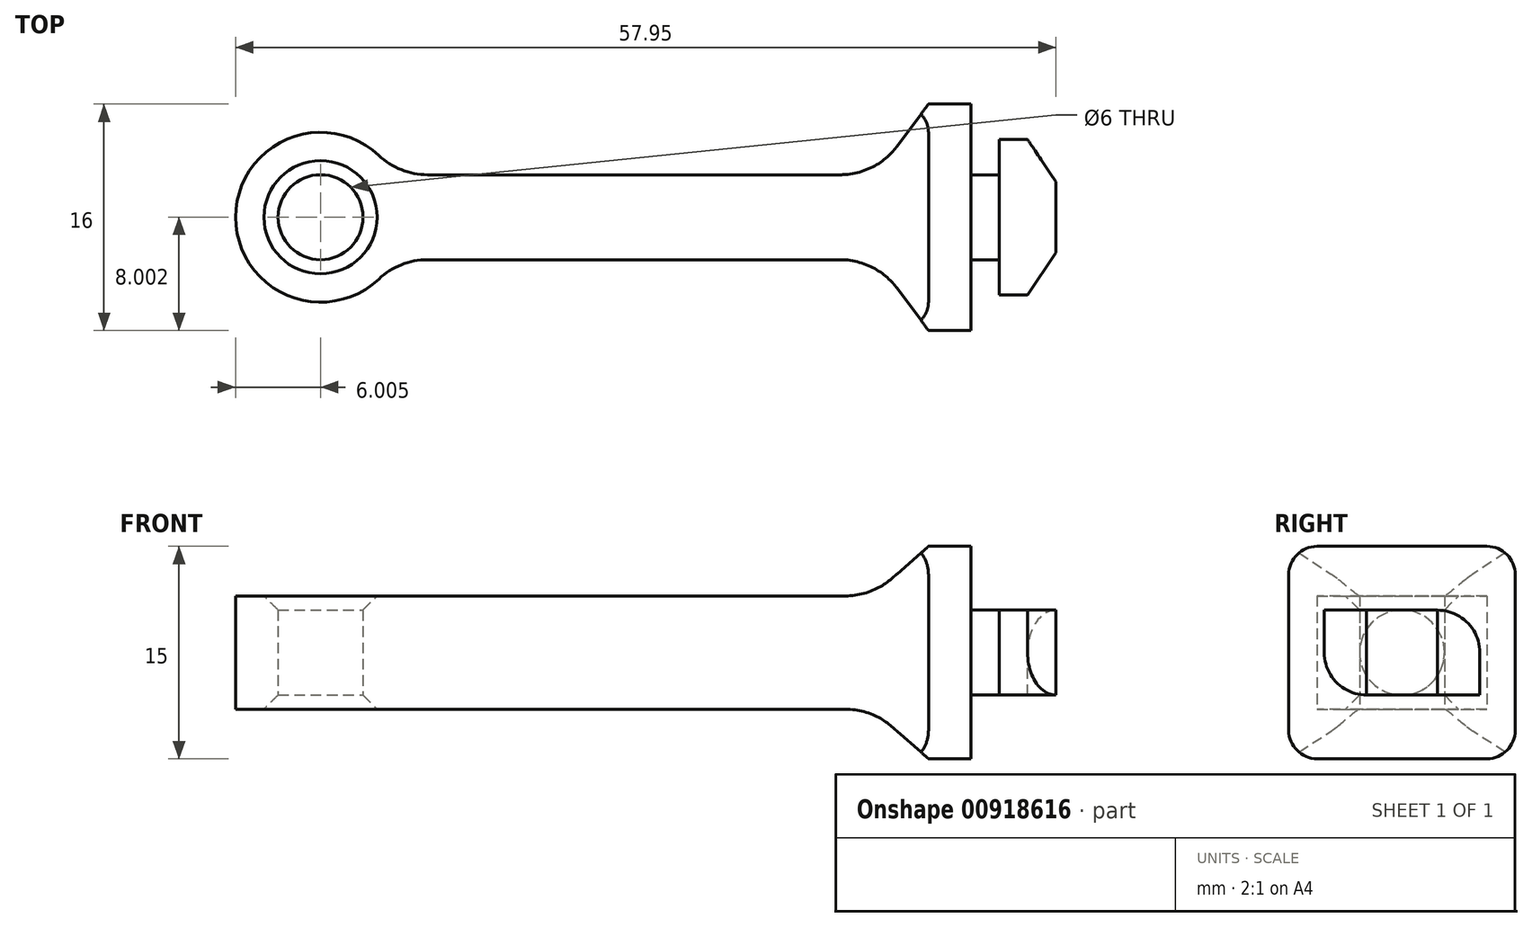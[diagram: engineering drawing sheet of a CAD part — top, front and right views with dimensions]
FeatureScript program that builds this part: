
annotation { "Feature Type Name" : "Feature", "Feature Type Description" : "" }
export const myFeature = defineFeature(function(context is Context, id is Id, definition is map)
    precondition{}
    {
        {
            var Q0;
            Q0=qCreatedBy(makeId("Top.planeOp"),FACE);
            var sketch = newSketch(context, id + "F0", { "sketchPlane" : qUnion([Q0])});
            skCircle(sketch, "E0", {"center": v(-45.95, 22.8) * mm, "radius": 3 * mm});
            skArc(sketch, "E1", {"start": v(-41.83, 27.16) * mm, "mid": v(-51.95, 22.8) * mm, "end": v(-41.83, 18.43) * mm});
            skLineSegment(sketch, "E2", {"start": v(0, 25.8) * mm, "end": v(0, 19.8) * mm});
            skLineSegment(sketch, "E3", {"start": v(-9.23, 19.8) * mm, "end": v(-38.4, 19.8) * mm});
            skLineSegment(sketch, "E4", {"start": v(-9.23, 25.8) * mm, "end": v(-38.4, 25.8) * mm});
            skLineSegment(sketch, "E5", {"start": v(-45.95, 22.8) * mm, "end": v(30.07, 22.8) * mm, "construction": true});
            skLineSegment(sketch, "E6", {"start": v(0, 25.8) * mm, "end": v(0, 30.8) * mm});
            skLineSegment(sketch, "E7", {"start": v(0, 30.8) * mm, "end": v(-3, 30.8) * mm});
            skLineSegment(sketch, "E8", {"start": v(-3, 30.8) * mm, "end": v(-5.22, 27.8) * mm});
            skLineSegment(sketch, "E9", {"start": v(0, 19.8) * mm, "end": v(0, 14.8) * mm});
            skLineSegment(sketch, "E10", {"start": v(0, 14.8) * mm, "end": v(-3, 14.8) * mm});
            skLineSegment(sketch, "E11", {"start": v(-3, 14.8) * mm, "end": v(-5.22, 17.78) * mm});
            skPoint(sketch, "E12.visualSharp", {"position": v(-6.72, 19.8) * mm});
            skArc(sketch, "E12.filletArc", {"start": v(-5.22, 17.78) * mm, "mid": v(-6.98, 19.26) * mm, "end": v(-9.23, 19.8) * mm});
            skPoint(sketch, "E13.visualSharp", {"position": v(-6.72, 25.8) * mm});
            skArc(sketch, "E13.filletArc", {"start": v(-9.23, 25.8) * mm, "mid": v(-6.98, 26.32) * mm, "end": v(-5.22, 27.8) * mm});
            skPoint(sketch, "E14.visualSharp", {"position": v(-40.75, 25.8) * mm});
            skArc(sketch, "E14.filletArc", {"start": v(-41.83, 27.16) * mm, "mid": v(-40.24, 26.15) * mm, "end": v(-38.4, 25.8) * mm});
            skPoint(sketch, "E15.visualSharp", {"position": v(-40.75, 19.8) * mm});
            skArc(sketch, "E15.filletArc", {"start": v(-38.4, 19.8) * mm, "mid": v(-40.24, 19.44) * mm, "end": v(-41.83, 18.43) * mm});
            skSolve(sketch);
        }
        {
            var Q0;
            Q0=makeQuery(id+"F0.imprint","IMPRINT",FACE,{"disambiguationData":[TD([[makeQuery(id+"F0.imprint","IMPRINT",EDGE,{"derivedFrom":sQuery(id+"F0.wireOp",EDGE,"E0")}),-1.0]])]});
            var Q1;
            Q1 = qSketchRegion(id + "F7BuKNyVjNSVHfz_0", true);
            extrude(context, id + "F1", {"entities" : qUnion([Q0, Q1]), "depth" : 15 * mm, "offsetDistance" : 25 * mm});
        }
        {
            var Q0;
            Q0=makeQuery(id+"F1.opExtrude","SWEPT_FACE",FACE,{"disambiguationData":[OSD([sQuery(id+"F0.wireOp",EDGE,"E2"),sQuery(id+"F0.wireOp",EDGE,"E6"),sQuery(id+"F0.wireOp",EDGE,"E9")])]});
            var sketch = newSketch(context, id + "F2", { "sketchPlane" : qUnion([Q0])});
            skCircle(sketch, "E16", {"center": v(22.8, 7.5) * mm, "radius": 3 * mm});
            skPoint(sketch, "E16.centerSnap0", {"position": v(22.8, 15) * mm});
            skPoint(sketch, "E16.centerSnap1", {"position": v(14.8, 7.5) * mm});
            skSolve(sketch);
        }
        {
            var Q0;
            Q0 = qSketchRegion(id + "F2", true);
            extrude(context, id + "F3", {"entities" : qUnion([Q0]), "operationType" : NewBodyOperationType.ADD, "depth" : 2 * mm, "offsetDistance" : 25 * mm});
        }
        {
            var Q0;
            Q0=makeQuery(id+"F3.opExtrude","CAP_FACE",FACE,{"disambiguationData":[OSD([sQuery(id+"F2.wireOp",EDGE,"E16")])],"isStart":false});
            var sketch = newSketch(context, id + "F4", { "sketchPlane" : qUnion([Q0])});
            skLineSegment(sketch, "E17.bottom", {"start": v(26.3, 4.5) * mm, "end": v(17.3, 4.5) * mm});
            skLineSegment(sketch, "E17.top", {"start": v(28.3, 10.5) * mm, "end": v(19.3, 10.5) * mm});
            skLineSegment(sketch, "E17.left", {"start": v(28.3, 6) * mm, "end": v(28.3, 10.5) * mm});
            skLineSegment(sketch, "E17.right", {"start": v(17.3, 4.5) * mm, "end": v(17.3, 9) * mm});
            skPoint(sketch, "E17.middle", {"position": v(22.8, 7.5) * mm});
            skPoint(sketch, "E18.orphan", {"position": v(28.3, 4.5) * mm});
            skPoint(sketch, "E19.orphan", {"position": v(17.3, 10.5) * mm});
            skLineSegment(sketch, "E20", {"start": v(17.3, 9) * mm, "end": v(17.3, 10.5) * mm});
            skLineSegment(sketch, "E21", {"start": v(19.3, 10.5) * mm, "end": v(17.3, 10.5) * mm});
            skLineSegment(sketch, "E22", {"start": v(26.3, 4.5) * mm, "end": v(28.3, 4.5) * mm});
            skLineSegment(sketch, "E23", {"start": v(28.3, 6) * mm, "end": v(28.3, 4.5) * mm});
            skSolve(sketch);
        }
        {
            var Q0;
            Q0 = qSketchRegion(id + "F4", true);
            extrude(context, id + "F5", {"entities" : qUnion([Q0]), "operationType" : NewBodyOperationType.ADD, "depth" : 4 * mm, "offsetDistance" : 25 * mm});
        }
        {
            var Q0;
            Q0=makeQuery(id+"F5.opExtrude","SWEPT_FACE",FACE,{"disambiguationData":[OSD([sQuery(id+"F4.wireOp",EDGE,"E17.bottom")])]});
            var sketch = newSketch(context, id + "F6", { "sketchPlane" : qUnion([Q0])});
            skLineSegment(sketch, "E24", {"start": v(4, -17.3) * mm, "end": v(6, -20.3) * mm});
            skSolve(sketch);
        }
        {
            var Q0;
            {var subQ0=sQuery(id+"F6.wireOp",EDGE,"E24");Q0=makeQuery(id+"F6.imprint","IMPRINT",FACE,{"disambiguationData":[TD([[makeQuery(id+"F6.imprint","IMPRINT",EDGE,{"derivedFrom":subQ0}),1.0]])]});}
            extrude(context, id + "F7", {"entities" : qUnion([Q0]), "operationType" : NewBodyOperationType.REMOVE, "oppositeDirection" : true, "depth" : 25 * mm, "offsetDistance" : 25 * mm});
        }
        {
            var Q0;
            Q0=makeQuery(id+"F5.opExtrude","SWEPT_FACE",FACE,{"disambiguationData":[OSD([sQuery(id+"F4.wireOp",EDGE,"E17.top")])]});
            var sketch = newSketch(context, id + "F8", { "sketchPlane" : qUnion([Q0])});
            skLineSegment(sketch, "E25", {"start": v(4, 28.3) * mm, "end": v(6, 25.3) * mm});
            skSolve(sketch);
        }
        {
            var Q0;
            {var subQ0=sQuery(id+"F8.wireOp",EDGE,"E25");Q0=makeQuery(id+"F8.imprint","IMPRINT",FACE,{"disambiguationData":[TD([[makeQuery(id+"F8.imprint","IMPRINT",EDGE,{"derivedFrom":subQ0}),1.0]])]});}
            extrude(context, id + "F9", {"entities" : qUnion([Q0]), "operationType" : NewBodyOperationType.REMOVE, "oppositeDirection" : true, "depth" : 25 * mm, "offsetDistance" : 25 * mm});
        }
        {
            var Q0;
            Q0=makeQuery(id+"F1.opExtrude","SWEPT_FACE",FACE,{"disambiguationData":[OSD([sQuery(id+"F0.wireOp",EDGE,"E10")])]});
            var sketch = newSketch(context, id + "F10", { "sketchPlane" : qUnion([Q0])});
            skLineSegment(sketch, "E26", {"start": v(-52.19, 11.5) * mm, "end": v(-8.88, 11.5) * mm});
            skLineSegment(sketch, "E27", {"start": v(-52.62, 3.5) * mm, "end": v(-8.88, 3.5) * mm});
            skPoint(sketch, "E28.start.orphan", {"position": v(-3, 7.5) * mm});
            skLineSegment(sketch, "E29", {"start": v(-3, 15) * mm, "end": v(-5.59, 12.74) * mm});
            skLineSegment(sketch, "E30", {"start": v(-3, 0) * mm, "end": v(-5.59, 2.26) * mm});
            skPoint(sketch, "E31.newPointA", {"position": v(-7, 11.5) * mm});
            skPoint(sketch, "E31.newPointB", {"position": v(-3, 11.5) * mm});
            skArc(sketch, "E31.filletArc", {"start": v(-8.88, 11.5) * mm, "mid": v(-7.12, 11.82) * mm, "end": v(-5.59, 12.74) * mm});
            skPoint(sketch, "E32.newPointA", {"position": v(-7, 3.5) * mm});
            skPoint(sketch, "E32.newPointB", {"position": v(-3, 3.5) * mm});
            skArc(sketch, "E32.filletArc", {"start": v(-5.59, 2.26) * mm, "mid": v(-7.12, 3.18) * mm, "end": v(-8.88, 3.5) * mm});
            skLineSegment(sketch, "E33", {"start": v(-52.19, 11.5) * mm, "end": v(-52.19, 19.96) * mm});
            skLineSegment(sketch, "E34", {"start": v(-52.19, 19.96) * mm, "end": v(-3, 19.96) * mm});
            skLineSegment(sketch, "E35", {"start": v(-3, 19.96) * mm, "end": v(-3, 15) * mm});
            skLineSegment(sketch, "E36", {"start": v(-52.62, 3.5) * mm, "end": v(-52.62, -5.04) * mm});
            skLineSegment(sketch, "E37", {"start": v(-52.62, -5.04) * mm, "end": v(-2.3, -5.04) * mm});
            skLineSegment(sketch, "E38", {"start": v(-2.3, -5.04) * mm, "end": v(-3, 0) * mm});
            skSolve(sketch);
        }
        {
            var Q0;
            Q0=makeQuery(id+"F10.imprint","IMPRINT",FACE,{"disambiguationData":[TD([[makeQuery(id+"F10.imprint","IMPRINT",EDGE,{"derivedFrom":sQuery(id+"F10.wireOp",EDGE,"E26")}),1.0]])]});
            var Q1;
            Q1=makeQuery(id+"F10.imprint","IMPRINT",FACE,{"disambiguationData":[TD([[makeQuery(id+"F10.imprint","IMPRINT",EDGE,{"derivedFrom":sQuery(id+"F10.wireOp",EDGE,"E27")}),-1.0]])]});
            extrude(context, id + "F11", {"entities" : qUnion([Q0, Q1]), "operationType" : NewBodyOperationType.REMOVE, "oppositeDirection" : true, "depth" : 25 * mm, "offsetDistance" : 25 * mm});
        }
        {
            var Q0;
            Q0=makeQuery(id+"F11.boolean.opBoolean","INTERSECT",EDGE,{"derivedFrom":[makeQuery(id+"F1.opExtrude","SWEPT_FACE",FACE,{"disambiguationData":[OSD([sQuery(id+"F0.wireOp",EDGE,"E0")])]}),makeQuery(id+"F11.opExtrude","SWEPT_FACE",FACE,{"disambiguationData":[OSD([sQuery(id+"F10.wireOp",EDGE,"E26")])]})]});
            chamfer(context, id + "F12", {"entities" : qUnion([Q0]), "width" : 1 * mm, "tangentPropagation" : true});
        }
        {
            var Q0;
            Q0=makeQuery(id+"F11.boolean.opBoolean","INTERSECT",EDGE,{"derivedFrom":[makeQuery(id+"F1.opExtrude","SWEPT_FACE",FACE,{"disambiguationData":[OSD([sQuery(id+"F0.wireOp",EDGE,"E0")])]}),makeQuery(id+"F11.opExtrude","SWEPT_FACE",FACE,{"disambiguationData":[OSD([sQuery(id+"F10.wireOp",EDGE,"E27")])]})]});
            chamfer(context, id + "F13", {"entities" : qUnion([Q0]), "width" : 1 * mm, "tangentPropagation" : true});
        }
        {
            var Q0;
            Q0=makeQuery(id+"F1.opExtrude","CAP_EDGE",EDGE,{"disambiguationData":[OSD([sQuery(id+"F0.wireOp",EDGE,"E10")])],"isStart":false});
            fillet(context, id + "F14", {"entities" : qUnion([Q0]), "radius" : 2 * mm, "tangentPropagation" : true, "allowEdgeOverflow" : false});
        }
        {
            var Q0;
            Q0=makeQuery(id+"F1.opExtrude","CAP_EDGE",EDGE,{"disambiguationData":[OSD([sQuery(id+"F0.wireOp",EDGE,"E7")])],"isStart":false});
            var Q1;
            Q1=makeQuery(id+"F1.opExtrude","CAP_EDGE",EDGE,{"disambiguationData":[OSD([sQuery(id+"F0.wireOp",EDGE,"E7")])],"isStart":true});
            var Q2;
            Q2=makeQuery(id+"F1.opExtrude","CAP_EDGE",EDGE,{"disambiguationData":[OSD([sQuery(id+"F0.wireOp",EDGE,"E10")])],"isStart":true});
            fillet(context, id + "F15", {"entities" : qUnion([Q0, Q1, Q2]), "radius" : 2 * mm, "tangentPropagation" : true, "allowEdgeOverflow" : false});
        }
        {
            var Q0;
            Q0=makeQuery(id+"F5.opExtrude","SWEPT_EDGE",EDGE,{"disambiguationData":[OSD([sQuery(id+"F4.wireOp",EDGE,"E17.bottom"),sQuery(id+"F4.wireOp",EDGE,"E17.right")])]});
            var Q1;
            Q1=makeQuery(id+"F5.opExtrude","SWEPT_EDGE",EDGE,{"disambiguationData":[OSD([sQuery(id+"F4.wireOp",EDGE,"E17.top"),sQuery(id+"F4.wireOp",EDGE,"E17.left")])]});
            fillet(context, id + "F16", {"entities" : qUnion([Q0, Q1]), "radius" : 3 * mm, "tangentPropagation" : true, "allowEdgeOverflow" : false});
        }
    });
